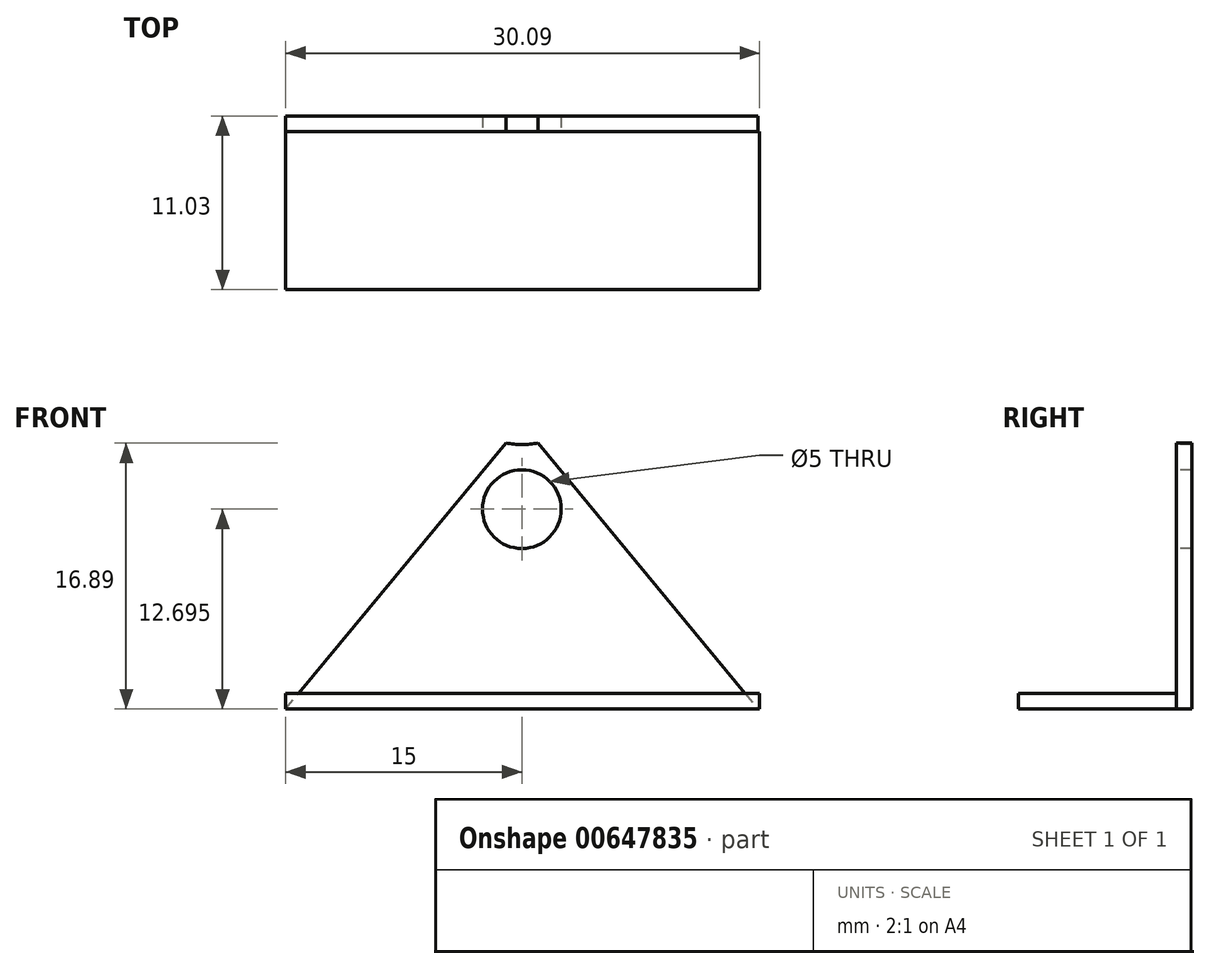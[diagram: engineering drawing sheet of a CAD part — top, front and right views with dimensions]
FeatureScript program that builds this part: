
annotation { "Feature Type Name" : "Feature", "Feature Type Description" : "" }
export const myFeature = defineFeature(function(context is Context, id is Id, definition is map)
    precondition{}
    {
        {
            var Q0;
            Q0=qCreatedBy(makeId("Front.planeOp"),FACE);
            var sketch = newSketch(context, id + "F0", { "sketchPlane" : qUnion([Q0])});
            skLineSegment(sketch, "E0.bottom", {"start": v(15, -9.06) * mm, "end": v(-15, -9.06) * mm});
            skPoint(sketch, "E0.middle", {"position": v(0, 0) * mm});
            skLineSegment(sketch, "E1", {"start": v(-15, -9.06) * mm, "end": v(0, 9.06) * mm});
            skLineSegment(sketch, "E2", {"start": v(0, 9.06) * mm, "end": v(15, -9.06) * mm});
            skPoint(sketch, "E3", {"position": v(0, 2.94) * mm});
            skSolve(sketch);
        }
        {
            var Q0;
            Q0=makeQuery(id+"F0.imprint","IMPRINT",FACE,{"disambiguationData":[TD([[makeQuery(id+"F0.imprint","IMPRINT",EDGE,{"derivedFrom":sQuery(id+"F0.wireOp",EDGE,"E0.bottom")}),-1.0]])]});
            extrude(context, id + "F1", {"entities" : qUnion([Q0]), "depth" : 1 * mm, "offsetDistance" : 25 * mm});
        }
        {
            var Q0;
            Q0=makeQuery(id+"F1.opExtrude","CAP_FACE",FACE,{"disambiguationData":[OSD([sQuery(id+"F0.wireOp",EDGE,"E0.bottom"),sQuery(id+"F0.wireOp",EDGE,"E1"),sQuery(id+"F0.wireOp",EDGE,"E2")])],"isStart":false});
            var sketch = newSketch(context, id + "F2", { "sketchPlane" : qUnion([Q0])});
            skPoint(sketch, "E4", {"position": v(0, 12.73) * mm});
            skSolve(sketch);
        }
        {
            var Q0;
            Q0=sQuery(id+"F2.wireOp",VERTEX,"E4");
            var Q1;
            Q1=makeQuery(id+"F1.opExtrude","SWEPT_BODY",BODY,{"disambiguationData":[OSD([sQuery(id+"F0.wireOp",EDGE,"E0.bottom"),sQuery(id+"F0.wireOp",EDGE,"E1"),sQuery(id+"F0.wireOp",EDGE,"E2")])]});
            hole(context, id + "F3", {"style" : HoleStyle.SIMPLE, "endStyle" : HoleEndStyle.THROUGH, "holeDiameter" : 10 * mm, "majorDiameter" : 5 * mm, "isTappedThrough" : true, "tappedDepth" : 12 * mm, "tapClearance" : 3, "locations" : qUnion([Q0]), "scope" : qUnion([Q1])});
        }
        {
            var Q0;
            Q0=makeQuery(id+"F1.opExtrude","SWEPT_FACE",FACE,{"disambiguationData":[OSD([sQuery(id+"F0.wireOp",EDGE,"E0.bottom")])]});
            var sketch = newSketch(context, id + "F4", { "sketchPlane" : qUnion([Q0])});
            skLineSegment(sketch, "E5.bottom", {"start": v(-15, 1) * mm, "end": v(15.1, 1) * mm});
            skLineSegment(sketch, "E5.top", {"start": v(-15, 11.03) * mm, "end": v(15.1, 11.03) * mm});
            skLineSegment(sketch, "E5.left", {"start": v(-15, 1) * mm, "end": v(-15, 11.03) * mm});
            skLineSegment(sketch, "E5.right", {"start": v(15.1, 1) * mm, "end": v(15.1, 11.03) * mm});
            skSolve(sketch);
        }
        {
            var Q0;
            Q0 = qSketchRegion(id + "F4", true);
            extrude(context, id + "F5", {"entities" : qUnion([Q0]), "operationType" : NewBodyOperationType.ADD, "oppositeDirection" : true, "depth" : 1 * mm, "offsetDistance" : 25 * mm});
        }
        {
            var Q0;
            Q0=makeQuery(id+"F1.opExtrude","CAP_FACE",FACE,{"disambiguationData":[OSD([sQuery(id+"F0.wireOp",EDGE,"E0.bottom"),sQuery(id+"F0.wireOp",EDGE,"E1"),sQuery(id+"F0.wireOp",EDGE,"E2")])],"isStart":false});
            var sketch = newSketch(context, id + "F6", { "sketchPlane" : qUnion([Q0])});
            skPoint(sketch, "E6", {"position": v(0, 3.63) * mm});
            skSolve(sketch);
        }
        {
            var Q0;
            Q0=sQuery(id+"F6.wireOp",VERTEX,"E6");
            var Q1;
            Q1=makeQuery(id+"F1.opExtrude","SWEPT_BODY",BODY,{"disambiguationData":[OSD([sQuery(id+"F0.wireOp",EDGE,"E0.bottom"),sQuery(id+"F0.wireOp",EDGE,"E1"),sQuery(id+"F0.wireOp",EDGE,"E2")])]});
            hole(context, id + "F7", {"style" : HoleStyle.SIMPLE, "endStyle" : HoleEndStyle.THROUGH, "holeDiameter" : 5 * mm, "majorDiameter" : 5 * mm, "isTappedThrough" : true, "tappedDepth" : 12 * mm, "tapClearance" : 3, "locations" : qUnion([Q0]), "scope" : qUnion([Q1])});
        }
    });
